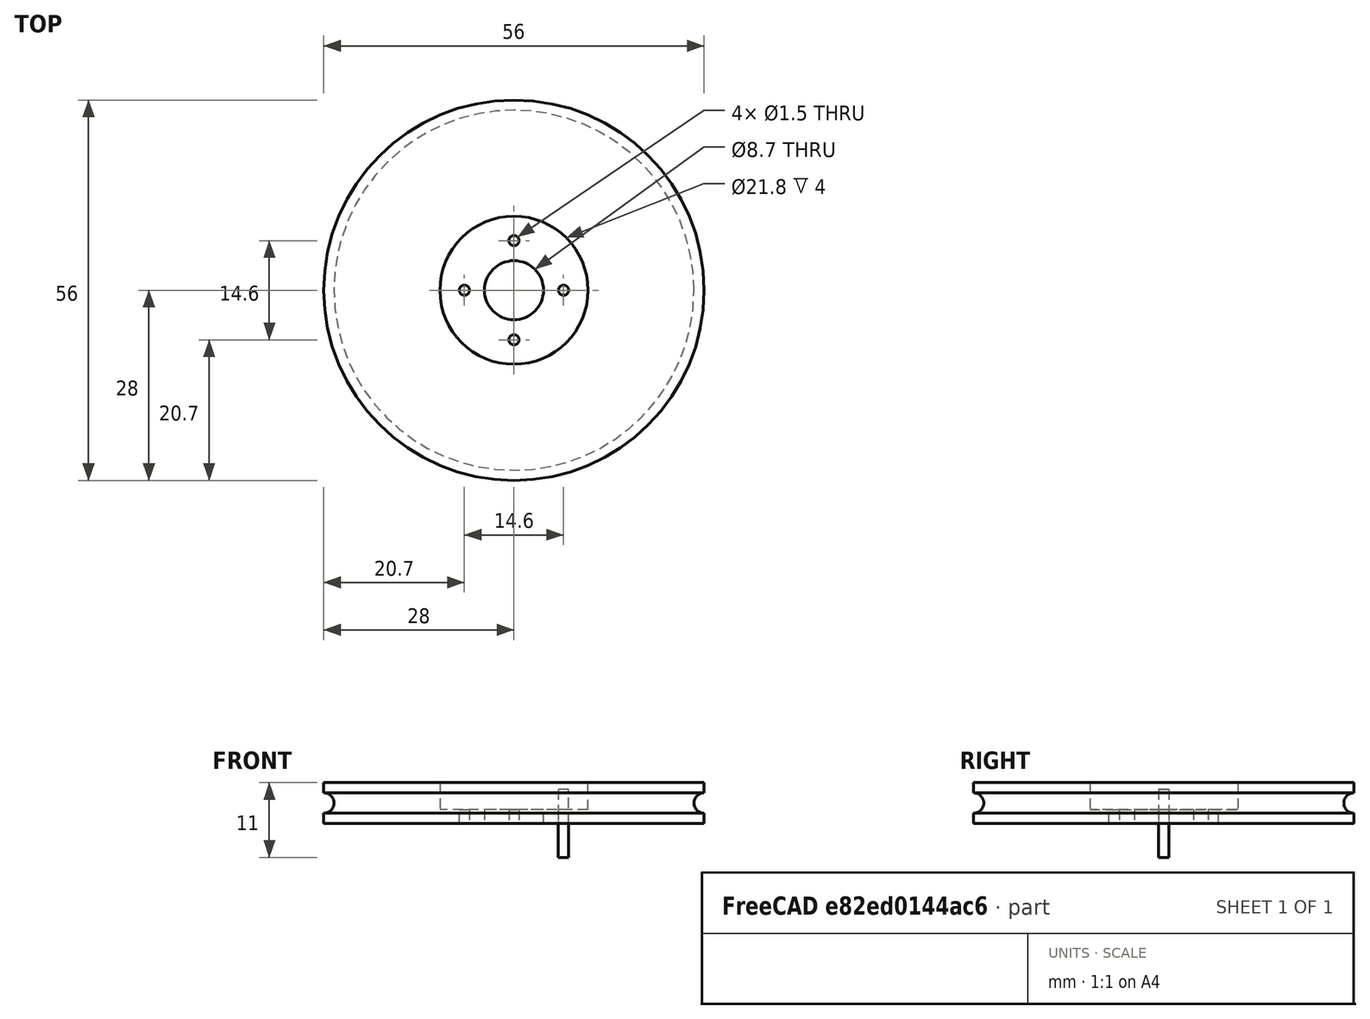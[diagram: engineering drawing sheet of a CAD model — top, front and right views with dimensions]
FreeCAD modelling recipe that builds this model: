
FCSTD DOCUMENT  (FreeCAD 0.21R33771 (Git))
Label: OJT1_T15P01_toros
License: All rights reserved
LicenseURL: http://en.wikipedia.org/wiki/All_rights_reserved
objects: Part::Cylinder×4, Part::Cut×4, Part::Torus×1, Part::FeaturePython×1
note: 9 computed .brp shape members not serialized (recipe doc carries the construction recipe); baked Part::Feature solids carry a one-line shape summary decoded from their .brp

FEATURE [Part::Torus] Torus  label="junta"
  Angle1 = -180
  Angle2 = 180
  Angle3 = 360
  AttacherType = Attacher::AttachEngine3D
  Placement = pos=(0,0,3) rot=(0,0,1;0rad)
  Radius1 = 28
  Radius2 = 1.5
FEATURE [Part::Cylinder] Cylinder  label="roda"
  Angle = 360
  AttacherType = Attacher::AttachEngine3D
  FirstAngle = 0
  Height = 6
  Radius = 28
  SecondAngle = 0
FEATURE [Part::Cut] Cut  label="roda amb junta"
  Base = -> Cylinder
  Refine = true
  Tool = -> Torus
FEATURE [Part::Cylinder] Cylinder001  label="corona servo"
  Angle = 360
  AttacherType = Attacher::AttachEngine3D
  FirstAngle = 0
  Height = 10
  Placement = pos=(0,0,2) rot=(0,0,1;0rad)
  Radius = 10.9
  SecondAngle = 0
FEATURE [Part::Cut] Cut001  label="roda amb junta i corona"
  Base = -> Cut
  Refine = true
  Tool = -> Cylinder001
FEATURE [Part::Cylinder] Cylinder002  label="forat eix"
  Angle = 360
  AttacherType = Attacher::AttachEngine3D
  FirstAngle = 0
  Height = 10
  Placement = pos=(0,0,-2) rot=(0,0,1;0rad)
  Radius = 4.35
  SecondAngle = 0
FEATURE [Part::Cut] Cut002  label="roda junta corona eix"
  Base = -> Cut001
  Refine = true
  Tool = -> Cylinder002
FEATURE [Part::Cylinder] Cylinder003  label="forat corona"
  Angle = 360
  AttacherType = Attacher::AttachEngine3D
  FirstAngle = 0
  Height = 10
  Placement = pos=(7.3,0,-5) rot=(0,0,1;0rad)
  Radius = 0.75
  SecondAngle = 0
FEATURE [Part::FeaturePython] Array  # Draft array (typed FeaturePython)
  AlwaysSyncPlacement = false
  Angle = 360
  ArrayType = 1
  Axis = (0,0,1)
  Base = -> Cylinder003
  Center = (0,0,1)
  Count = 4
  ExpandArray = false
  Fuse = false
  IntervalAxis = (0,0,0)
  IntervalX = (50,0,0)
  IntervalY = (0,50,0)
  IntervalZ = (0,0,50)
  NumberCircles = 3
  NumberPolar = 4
  NumberX = 2
  NumberY = 2
  NumberZ = 1
  PlacementList = 4 placements: [(7.3,0,-5),(1.62093e-15,7.3,-5),(-7.3,8.93992e-16,-5),(-1.62093e-15,-7.3,-5)]
  RadialDistance = 50
  ScaleList = (4) [(1,1,1),(1,1,1),(1,1,1),(1,1,1)]
  Symmetry = 1
  TangentialDistance = 25
FEATURE [Part::Cut] Cut003  label="roda miniskybot"
  Base = -> Cut002
  Refine = true
  Tool = -> Array
